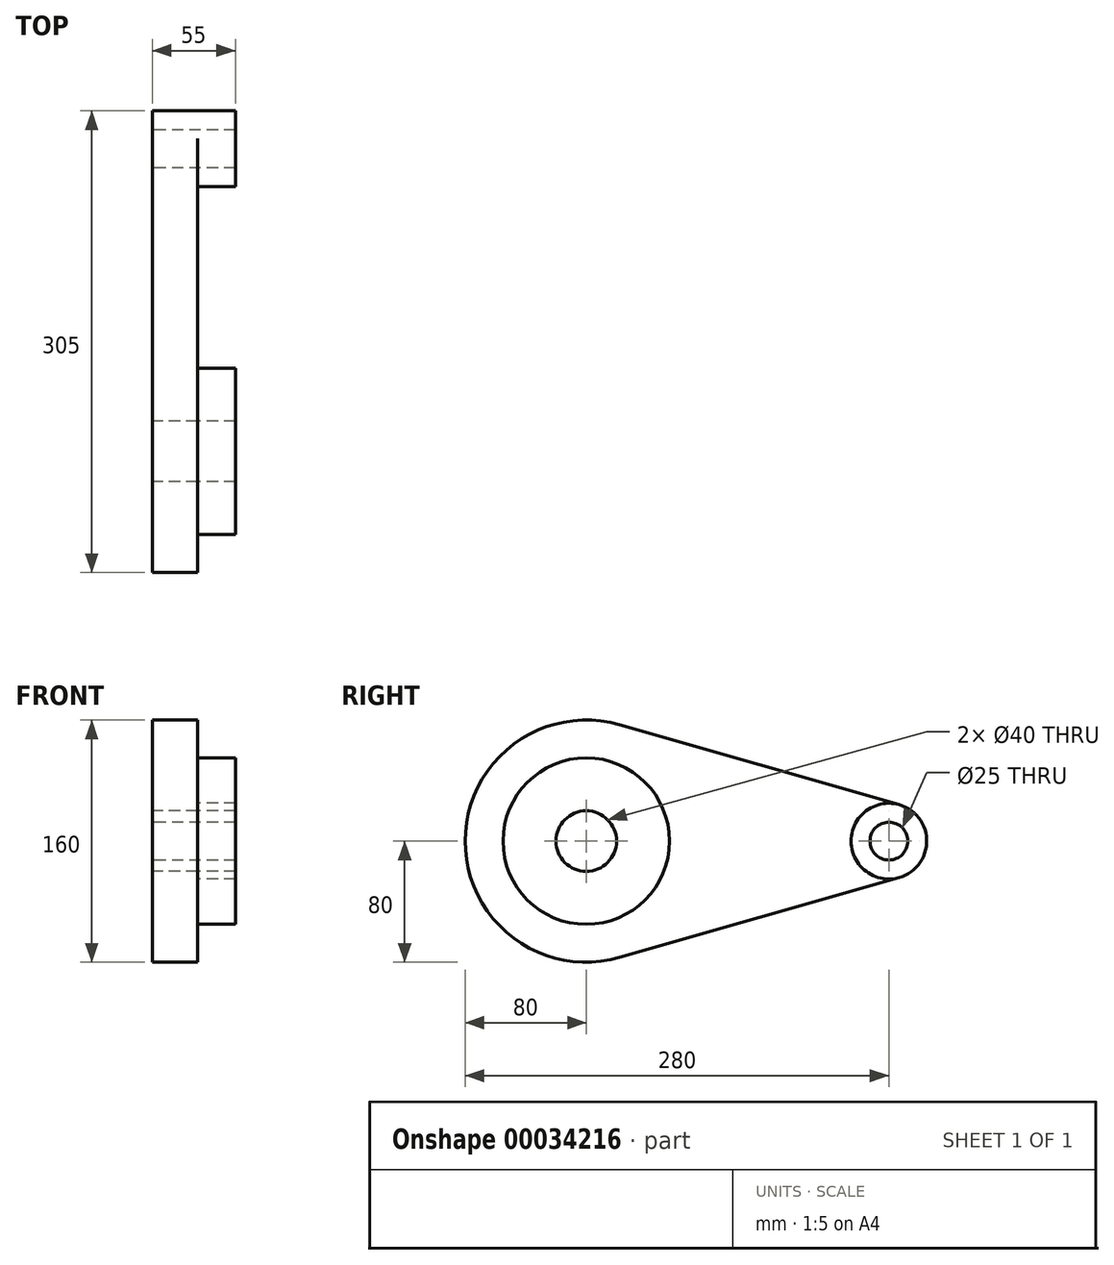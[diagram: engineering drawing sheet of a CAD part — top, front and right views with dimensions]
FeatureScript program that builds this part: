
annotation { "Feature Type Name" : "Feature", "Feature Type Description" : "" }
export const myFeature = defineFeature(function(context is Context, id is Id, definition is map)
    precondition{}
    {
        {
            var Q0;
            Q0=qCreatedBy(makeId("Right.planeOp"),FACE);
            var sketch = newSketch(context, id + "F0", { "sketchPlane" : qUnion([Q0])});
            skCircle(sketch, "E0", {"center": v(0, 0) * mm, "radius": 80 * mm});
            skCircle(sketch, "E1", {"center": v(200, 0) * mm, "radius": 25 * mm});
            skLineSegment(sketch, "E2", {"start": v(22, 76.92) * mm, "end": v(206.88, 24.04) * mm});
            skCircle(sketch, "E3", {"center": v(0, 0) * mm, "radius": 20 * mm});
            skCircle(sketch, "E4", {"center": v(200, 0) * mm, "radius": 12.5 * mm});
            skLineSegment(sketch, "E5", {"start": v(22, -76.92) * mm, "end": v(206.88, -24.04) * mm});
            skSolve(sketch);
        }
        {
            var Q0;
            Q0=makeQuery(id+"F0.imprint","IMPRINT",FACE,{"disambiguationData":[TD([[makeQuery(id+"F0.imprint","IMPRINT",EDGE,{"derivedFrom":sQuery(id+"F0.wireOp",EDGE,"E3")}),-1.0]])]});
            var Q1;
            {var subQ1=sQuery(id+"F0.wireOp",EDGE,"E2");Q1=makeQuery(id+"F0.imprint","IMPRINT",FACE,{"disambiguationData":[TD([[makeQuery(id+"F0.imprint","IMPRINT",EDGE,{"derivedFrom":subQ1}),-1.0]])]});}
            var Q2;
            Q2=makeQuery(id+"F0.imprint","IMPRINT",FACE,{"disambiguationData":[TD([[makeQuery(id+"F0.imprint","IMPRINT",EDGE,{"derivedFrom":sQuery(id+"F0.wireOp",EDGE,"E4")}),-1.0]])]});
            extrude(context, id + "F1", {"entities" : qUnion([Q0, Q1, Q2]), "depth" : 30 * mm});
        }
        {
            var Q0;
            Q0=makeQuery(id+"F1.opExtrude","CAP_FACE",FACE,{"disambiguationData":[OSD([sQuery(id+"F0.wireOp",EDGE,"E0"),sQuery(id+"F0.wireOp",EDGE,"E1"),sQuery(id+"F0.wireOp",EDGE,"E2"),sQuery(id+"F0.wireOp",EDGE,"E3"),sQuery(id+"F0.wireOp",EDGE,"E4"),sQuery(id+"F0.wireOp",EDGE,"E5")])],"isStart":false});
            var sketch = newSketch(context, id + "F2", { "sketchPlane" : qUnion([Q0])});
            skCircle(sketch, "E6", {"center": v(0, 0) * mm, "radius": 55 * mm});
            skCircle(sketch, "E7", {"center": v(200, 0) * mm, "radius": 25 * mm});
            skSolve(sketch);
        }
        {
            var Q0;
            Q0=makeQuery(id+"F2.imprint","IMPRINT",FACE,{"disambiguationData":[TD([[makeQuery(id+"F2.imprint","IMPRINT",EDGE,{"derivedFrom":sQuery(id+"F2.wireOp",EDGE,"E6")}),1.0]])]});
            var Q1;
            Q1=sQuery(id+"F2.wireOp",EDGE,"E6");
            extrude(context, id + "F3", {"entities" : qUnion([Q0]), "surfaceEntities" : qUnion([Q1]), "depth" : 25 * mm});
        }
        {
            var Q0;
            Q0=makeQuery(id+"F1.opExtrude","CAP_FACE",FACE,{"disambiguationData":[OSD([sQuery(id+"F0.wireOp",EDGE,"E0"),sQuery(id+"F0.wireOp",EDGE,"E1"),sQuery(id+"F0.wireOp",EDGE,"E2"),sQuery(id+"F0.wireOp",EDGE,"E3"),sQuery(id+"F0.wireOp",EDGE,"E4"),sQuery(id+"F0.wireOp",EDGE,"E5")])],"isStart":false});
            var sketch = newSketch(context, id + "F4", { "sketchPlane" : qUnion([Q0])});
            skCircle(sketch, "E8", {"center": v(200, 0) * mm, "radius": 25 * mm});
            skSolve(sketch);
        }
        {
            var Q0;
            Q0=makeQuery(id+"F4.imprint","IMPRINT",FACE,{"disambiguationData":[TD([[makeQuery(id+"F4.imprint","IMPRINT",EDGE,{"derivedFrom":makeQuery(id+"F1.opExtrude","CAP_EDGE",EDGE,{"disambiguationData":[OSD([sQuery(id+"F0.wireOp",EDGE,"E4")])],"isStart":false})}),-1.0]])]});
            extrude(context, id + "F5", {"entities" : qUnion([Q0]), "operationType" : NewBodyOperationType.ADD, "depth" : 25 * mm});
        }
    });
